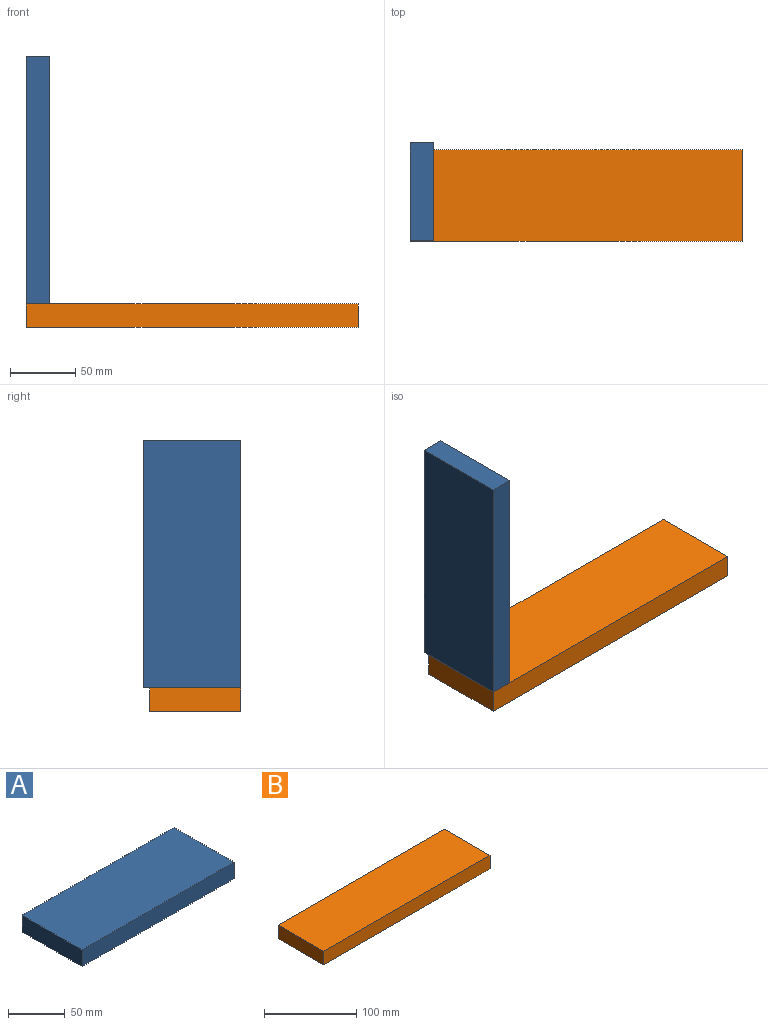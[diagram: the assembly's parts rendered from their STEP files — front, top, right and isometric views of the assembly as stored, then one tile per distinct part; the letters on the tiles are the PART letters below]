
ASSEMBLY  parts=2 mates=1
PART A: 6 faces, bbox 190x75x18 mm
  f0: plane 75x18mm, normal (-1,0,0), area 1350mm2, adj f1,f3,f4,f5
  f1: plane 190x18mm, normal (0,-1,0), area 3420mm2, adj f0,f2,f4,f5
  f2: plane 75x18mm, normal (1,0,0), area 1350mm2, adj f1,f3,f4,f5
  f3: plane 190x18mm, normal (0,1,0), area 3420mm2, adj f0,f2,f4,f5
  f4: plane 190x75mm, normal (0,0,1), area 14250mm2, adj f0,f1,f2,f3
  f5: plane 190x75mm, normal (0,0,-1), area 14250mm2, adj f0,f1,f2,f3
PART B: 6 faces, bbox 255x70x18 mm
  f0: plane 70x18mm, normal (-1,0,0), area 1260mm2, adj f1,f3,f4,f5
  f1: plane 255x18mm, normal (0,-1,0), area 4590mm2, adj f0,f2,f4,f5
  f2: plane 70x18mm, normal (1,0,0), area 1260mm2, adj f1,f3,f4,f5
  f3: plane 255x18mm, normal (0,1,0), area 4590mm2, adj f0,f2,f4,f5
  f4: plane 255x70mm, normal (0,0,1), area 17850mm2, adj f0,f1,f2,f3
  f5: plane 255x70mm, normal (0,0,-1), area 17850mm2, adj f0,f1,f2,f3
PLACE A rot(axis=(0,-1,0),90deg) t=(137.75,0,-109.96)mm
PLACE B t=(119.75,0,-127.96)mm
MATE fastened B.f1 <-> A.f1  axis (0,-1,0) through (119.75,0,-109.96)mm
